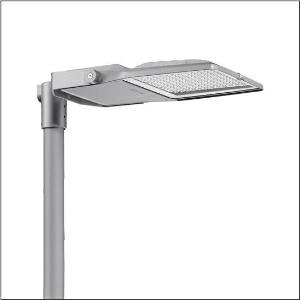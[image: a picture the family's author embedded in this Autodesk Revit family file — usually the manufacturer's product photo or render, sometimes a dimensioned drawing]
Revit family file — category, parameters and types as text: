
# Revit family: floodlight_fl_21_midi___pl33t_5xa7786e2f3a_2de9
name_source: partatom
category: Lighting Fixtures
units: mm (PartAtom-declared; Revit-internal decimal feet)

## family parameters
Cut with Voids When Loaded = No
Host = Face
Light Source = No
Part Type = Normal
Room Calculation Point = No
Round Connector Dimension = Use Diameter
Shared = No

## types (1)
- --- (1 x LED, 26630 lm, 212.4 W, 3000K)
    Apparent Load = 212 VA
    CIE Flux Codes = 26 75 99 100 100
    Color Rendering = 70
    Color Temperature = 3000K
    Default Elevation = 1800 mm
    Description = Floodlight FL 21 midi, floodlight, primary light control with lens, of PMMA, primary optical cover: protective disc, of toughened safety glass, transparent, light distribution: PL33T, light emission: direct distribution, installation type: surface-mounted, LED, High Power LED, rated luminous flux: 26.630lm, luminous efficacy: 125lm/W, light colour: 730, colour temperature: 3000K, control gear: ECG Smart Interface, control: flexible luminous flux parameterisation, time-dependent luminous flux control, constant luminous flux control, overheat protection, pre-setting: logarithmic dimming characteristic, with terminal, 6-pole, mains connection: 220..240V, AC, 50/60Hz, start of lifetime: 212W, end of service life: 231W, reduction: 95W, luminaire housing, of diecast aluminium, powder-coated, Siteco® metallic grey (DB 702S), corrosivity category C5 mid according to DIN EN ISO 12944, sealing non-destructively replaceable, please order mast flange separately, mast bracket, of steel, galvanised, powder-coated, Siteco® metallic grey (DB 702S), Smart Interface below and above, protection rating (complete): IP66, insulation class (complete): insulation class II (safety insulation), certification: CE, ENEC, VDE, protection symbol: D, impact resistance: IK08, permissible operating ambient temperature: -40..+40°C, permissible operating ambient temperature for outdoor applications: -40..+50°C, standard: DIN EN 12944, LABS conformity tested according to VDMA 24364:2018-05, packaging unit: 1 piece

Light Distribution: PL33T
    Height = 76 mm
    Lamp = 1 x LED
    Lamp Light Flux = 26630 lm
    Lamp Power = 212.4 W
    Lamp count = 1
    Length = 657 mm
    Luminous efficacy = 125 lm/W
    Manufacturer = Siteco
    ModVariant = No
    Model = 5XA7786E2F3A
    Number of Poles = 1
    OnlyDefault = Yes
    Power Factor = 1
    Product Name = Floodlight FL 21 midi | PL33T
    Product group = floodlight | pylon annexe
    ProductGroupID = 6200
    Protection Class = Protection class II
    Protection Degree = IP 66
    RLX_Detail_Level = 1
    RLX_Emergency_Light_Flux = 0 lm
    RLX_Emergency_Type = 0
    RLX_Emergency_Type_DB = No
    RlxData = <blob elided: 153605 chars, md5=816cf59d>
    Socket = socket
    Standby Power = 0 W
    System Light Flux = 26630 lm
    System Power = 212 W
    Type Comments = factory setting: luminous flux: 100 % | dim-lin: 254 | 710 mA
    Type Image = l_1007123.jpg
    URL = http://relux.com
    VarID = @adj_120877
    Voltage = 0 V
    Weight = 0.00 kg
    Width = 442 mm

## geometry (parser evidence)
native form markers: Blend x4, Sweep x15
no freeform markers — native parametric forms only
